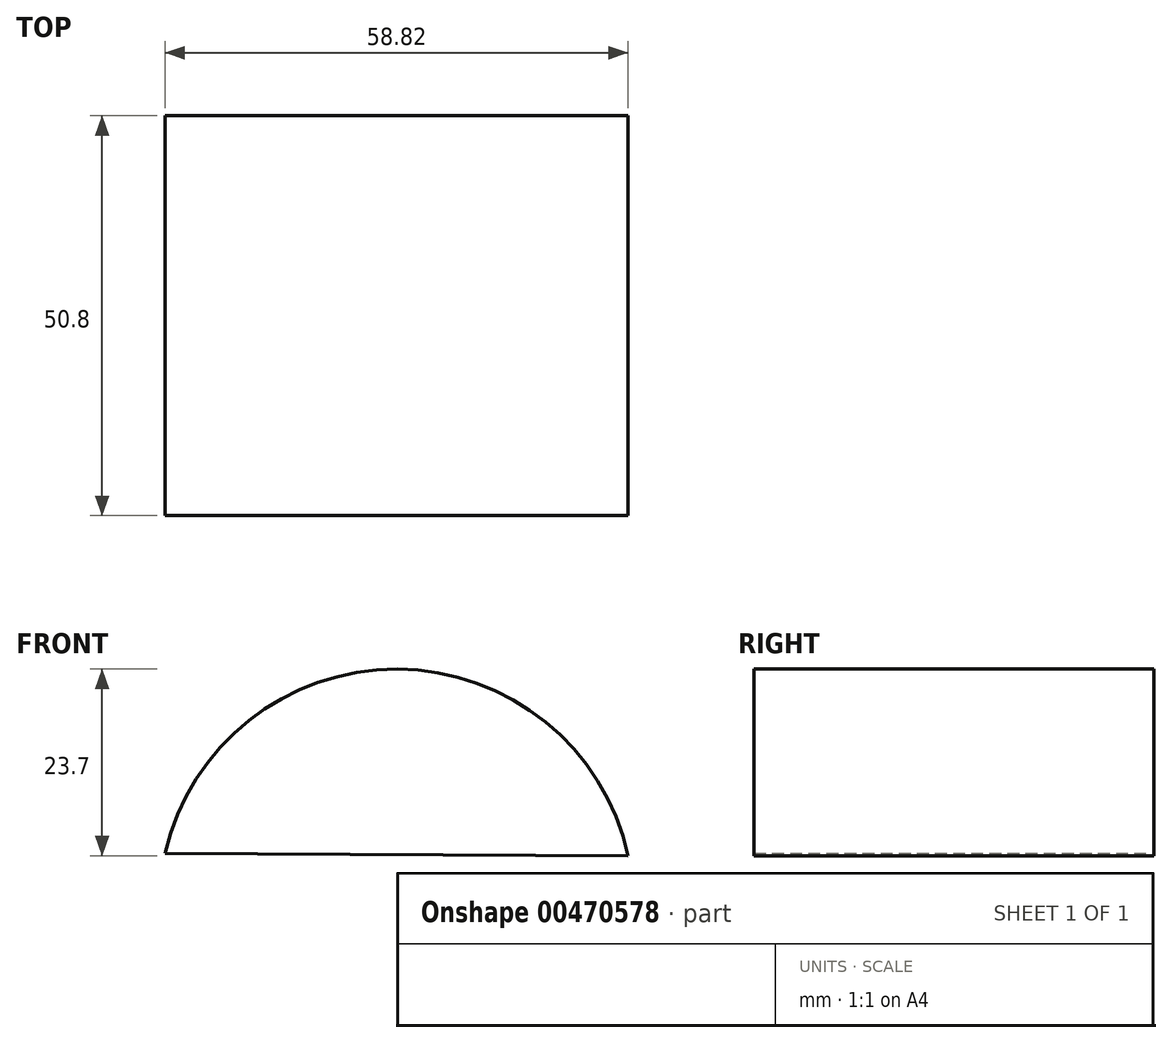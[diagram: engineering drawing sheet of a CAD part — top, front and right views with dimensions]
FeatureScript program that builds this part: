
annotation { "Feature Type Name" : "Feature", "Feature Type Description" : "" }
export const myFeature = defineFeature(function(context is Context, id is Id, definition is map)
    precondition{}
    {
        {
            var Q0;
            Q0=qCreatedBy(makeId("Front.planeOp"),FACE);
            var sketch = newSketch(context, id + "F0", { "sketchPlane" : qUnion([Q0])});
            skArc(sketch, "E0", {"start": v(-9.06, 25.65) * mm, "mid": v(-38.36, 49.35) * mm, "end": v(-67.88, 25.93) * mm});
            skLineSegment(sketch, "E1", {"start": v(-67.88, 25.93) * mm, "end": v(-9.06, 25.65) * mm});
            skSolve(sketch);
        }
        {
            var Q0;
            Q0 = qSketchRegion(id + "F0", true);
            extrude(context, id + "F1", {"entities" : qUnion([Q0]), "depth" : 50.8 * mm});
        }
    });
